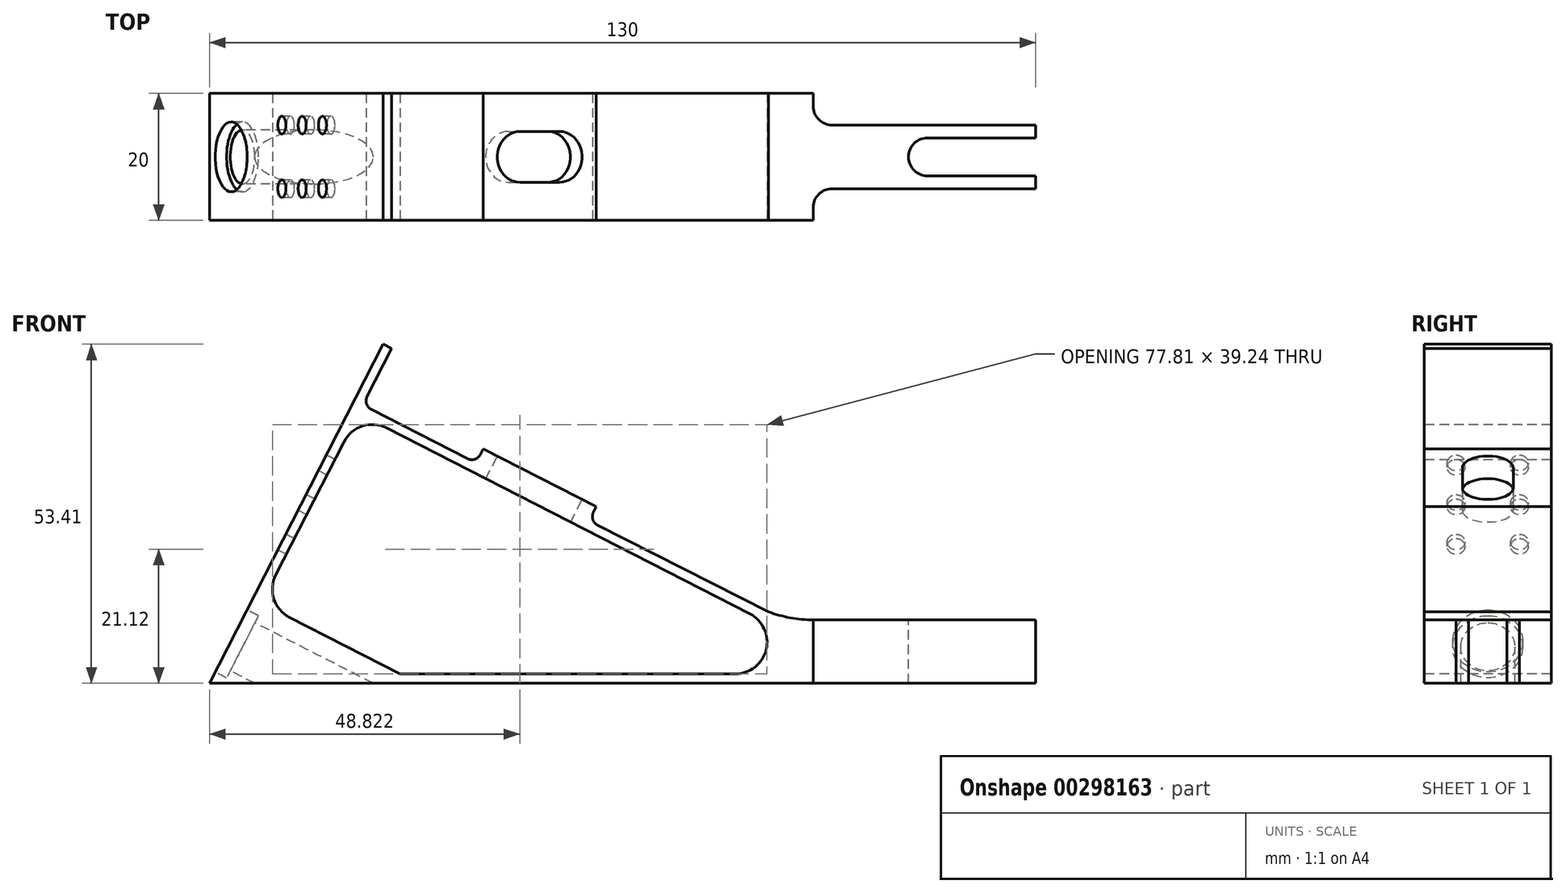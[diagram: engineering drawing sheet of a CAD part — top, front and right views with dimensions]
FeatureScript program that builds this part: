
annotation { "Feature Type Name" : "Feature", "Feature Type Description" : "" }
export const myFeature = defineFeature(function(context is Context, id is Id, definition is map)
    precondition{}
    {
        {
            var Q0;
            Q0=qCreatedBy(makeId("Front.planeOp"),FACE);
            var sketch = newSketch(context, id + "F0", { "sketchPlane" : qUnion([Q0])});
            skLineSegment(sketch, "E0", {"start": v(0, 0) * mm, "end": v(130, 0) * mm});
            skLineSegment(sketch, "E1", {"start": v(130, 0) * mm, "end": v(130, 10) * mm});
            skLineSegment(sketch, "E2", {"start": v(130, 10) * mm, "end": v(95, 10) * mm});
            skArc(sketch, "E3", {"start": v(95, 10) * mm, "mid": v(91.42, 10.32) * mm, "end": v(87.96, 11.28) * mm});
            skLineSegment(sketch, "E4", {"start": v(0, 0) * mm, "end": v(27.35, 53.4) * mm});
            skLineSegment(sketch, "E5", {"start": v(27.35, 53.4) * mm, "end": v(28.68, 52.72) * mm});
            skLineSegment(sketch, "E6", {"start": v(28.68, 52.72) * mm, "end": v(24.12, 43.82) * mm});
            skLineSegment(sketch, "E7", {"start": v(24.12, 43.82) * mm, "end": v(41.93, 34.7) * mm});
            skLineSegment(sketch, "E8", {"start": v(41.93, 34.7) * mm, "end": v(43.06, 36.93) * mm});
            skLineSegment(sketch, "E9", {"start": v(43.06, 36.93) * mm, "end": v(60.87, 27.82) * mm});
            skLineSegment(sketch, "E10", {"start": v(59.73, 25.6) * mm, "end": v(87.96, 11.28) * mm});
            skLineSegment(sketch, "E11", {"start": v(60.87, 27.82) * mm, "end": v(59.73, 25.6) * mm});
            skSolve(sketch);
        }
        {
            var Q0;
            Q0 = qSketchRegion(id + "F0", true);
            extrude(context, id + "F1", {"entities" : qUnion([Q0]), "depth" : 20 * mm});
        }
        {
            var Q0;
            Q0=makeQuery(id+"F1.opExtrude","SWEPT_EDGE",EDGE,{"disambiguationData":[OSD([sQuery(id+"F0.wireOp",EDGE,"E10"),sQuery(id+"F0.wireOp",EDGE,"E11")])]});
            var Q1;
            Q1=makeQuery(id+"F1.opExtrude","SWEPT_EDGE",EDGE,{"disambiguationData":[OSD([sQuery(id+"F0.wireOp",EDGE,"E6"),sQuery(id+"F0.wireOp",EDGE,"E7")])]});
            var Q2;
            Q2=makeQuery(id+"F1.opExtrude","SWEPT_EDGE",EDGE,{"disambiguationData":[OSD([sQuery(id+"F0.wireOp",EDGE,"E7"),sQuery(id+"F0.wireOp",EDGE,"E8")])]});
            fillet(context, id + "F2", {"entities" : qUnion([Q0, Q1, Q2]), "radius" : 1.5 * mm, "tangentPropagation" : true, "allowEdgeOverflow" : false});
        }
        {
            var Q0;
            Q0=makeQuery(id+"F1.opExtrude","SWEPT_FACE",FACE,{"disambiguationData":[OSD([sQuery(id+"F0.wireOp",EDGE,"E2")])]});
            var sketch = newSketch(context, id + "F3", { "sketchPlane" : qUnion([Q0])});
            skLineSegment(sketch, "E12.bottom", {"start": v(130, 0) * mm, "end": v(95, 0) * mm});
            skLineSegment(sketch, "E12.top", {"start": v(130, -5) * mm, "end": v(95, -5) * mm});
            skLineSegment(sketch, "E12.left", {"start": v(130, 0) * mm, "end": v(130, -5) * mm});
            skLineSegment(sketch, "E12.right", {"start": v(95, 0) * mm, "end": v(95, -5) * mm});
            skLineSegment(sketch, "E13.bottom", {"start": v(130, -20) * mm, "end": v(95, -20) * mm});
            skLineSegment(sketch, "E13.top", {"start": v(130, -15) * mm, "end": v(95, -15) * mm});
            skLineSegment(sketch, "E13.left", {"start": v(130, -20) * mm, "end": v(130, -15) * mm});
            skLineSegment(sketch, "E13.right", {"start": v(95, -20) * mm, "end": v(95, -15) * mm});
            skSolve(sketch);
        }
        {
            var Q0;
            Q0=makeQuery(id+"F3.imprint","IMPRINT",FACE,{"disambiguationData":[TD([[makeQuery(id+"F3.imprint","IMPRINT",EDGE,{"derivedFrom":sQuery(id+"F3.wireOp",EDGE,"E12.bottom")}),1.0]])]});
            var Q1;
            Q1=makeQuery(id+"F3.imprint","IMPRINT",FACE,{"disambiguationData":[TD([[makeQuery(id+"F3.imprint","IMPRINT",EDGE,{"derivedFrom":sQuery(id+"F3.wireOp",EDGE,"E13.bottom")}),-1.0]])]});
            extrude(context, id + "F4", {"entities" : qUnion([Q0, Q1]), "operationType" : NewBodyOperationType.REMOVE, "endBound" : BoundingType.THROUGH_ALL, "oppositeDirection" : true, "depth" : 25 * mm});
        }
        {
            var Q0;
            Q0=makeQuery(id+"F4.boolean.opBoolean","COPY",EDGE,{"derivedFrom":makeQuery(id+"F4.opExtrude","SWEPT_EDGE",EDGE,{"disambiguationData":[OSD([sQuery(id+"F0.wireOp",EDGE,"E2"),sQuery(id+"F0.wireOp",EDGE,"E3"),sQuery(id+"F3.wireOp",EDGE,"E13.top"),sQuery(id+"F3.wireOp",EDGE,"E13.right")])]})});
            var Q1;
            Q1=makeQuery(id+"F4.boolean.opBoolean","COPY",EDGE,{"derivedFrom":makeQuery(id+"F4.opExtrude","SWEPT_EDGE",EDGE,{"disambiguationData":[OSD([sQuery(id+"F0.wireOp",EDGE,"E2"),sQuery(id+"F0.wireOp",EDGE,"E3"),sQuery(id+"F3.wireOp",EDGE,"E12.top"),sQuery(id+"F3.wireOp",EDGE,"E12.right")])]})});
            fillet(context, id + "F5", {"entities" : qUnion([Q0, Q1]), "radius" : 3 * mm, "tangentPropagation" : true, "allowEdgeOverflow" : false});
        }
        {
            var Q0;
            Q0=makeQuery(id+"F1.opExtrude","SWEPT_FACE",FACE,{"disambiguationData":[OSD([sQuery(id+"F0.wireOp",EDGE,"E2")])]});
            var sketch = newSketch(context, id + "F6", { "sketchPlane" : qUnion([Q0])});
            skLineSegment(sketch, "E14.bottom", {"start": v(130, -7) * mm, "end": v(113, -7) * mm});
            skLineSegment(sketch, "E14.top", {"start": v(130, -13) * mm, "end": v(113, -13) * mm});
            skLineSegment(sketch, "E14.left", {"start": v(130, -7) * mm, "end": v(130, -13) * mm});
            skArc(sketch, "E15", {"start": v(113, -13) * mm, "mid": v(110, -10) * mm, "end": v(113, -7) * mm});
            skSolve(sketch);
        }
        {
            var Q0;
            Q0=makeQuery(id+"F6.imprint","IMPRINT",FACE,{"disambiguationData":[TD([[makeQuery(id+"F6.imprint","IMPRINT",EDGE,{"derivedFrom":sQuery(id+"F6.wireOp",EDGE,"E14.bottom")}),1.0]])]});
            extrude(context, id + "F7", {"entities" : qUnion([Q0]), "operationType" : NewBodyOperationType.REMOVE, "endBound" : BoundingType.THROUGH_ALL, "oppositeDirection" : true, "depth" : 25 * mm});
        }
        {
            var Q0;
            Q0=makeQuery(id+"F1.opExtrude","SWEPT_FACE",FACE,{"disambiguationData":[OSD([sQuery(id+"F0.wireOp",EDGE,"E9")])]});
            var sketch = newSketch(context, id + "F8", { "sketchPlane" : qUnion([Q0])});
            skLineSegment(sketch, "E16", {"start": v(-33.5, -10) * mm, "end": v(68.03, -10) * mm, "construction": true});
            skPoint(sketch, "E16.startSnap0", {"position": v(21.5, -10) * mm});
            skLineSegment(sketch, "E17", {"start": v(28, -6) * mm, "end": v(35, -6) * mm});
            skLineSegment(sketch, "E18", {"start": v(28, -14) * mm, "end": v(35, -14) * mm});
            skArc(sketch, "E19", {"start": v(28, -6) * mm, "mid": v(24, -10) * mm, "end": v(28, -14) * mm});
            skArc(sketch, "E20", {"start": v(35, -6) * mm, "mid": v(39, -10) * mm, "end": v(35, -14) * mm});
            skSolve(sketch);
        }
        {
            var Q0;
            Q0 = qSketchRegion(id + "F8", true);
            extrude(context, id + "F9", {"entities" : qUnion([Q0]), "operationType" : NewBodyOperationType.REMOVE, "oppositeDirection" : true, "depth" : 4 * mm});
        }
        {
            var Q0;
            Q0=makeQuery(id+"F1.opExtrude","CAP_FACE",FACE,{"disambiguationData":[OSD([sQuery(id+"F0.wireOp",EDGE,"E0"),sQuery(id+"F0.wireOp",EDGE,"E1"),sQuery(id+"F0.wireOp",EDGE,"E2"),sQuery(id+"F0.wireOp",EDGE,"E3"),sQuery(id+"F0.wireOp",EDGE,"E4"),sQuery(id+"F0.wireOp",EDGE,"E5"),sQuery(id+"F0.wireOp",EDGE,"E6"),sQuery(id+"F0.wireOp",EDGE,"E7"),sQuery(id+"F0.wireOp",EDGE,"E8"),sQuery(id+"F0.wireOp",EDGE,"E9"),sQuery(id+"F0.wireOp",EDGE,"E10"),sQuery(id+"F0.wireOp",EDGE,"E11")])],"isStart":false});
            var sketch = newSketch(context, id + "F10", { "sketchPlane" : qUnion([Q0])});
            skLineSegment(sketch, "E21", {"start": v(21.16, 38.04) * mm, "end": v(10.45, 17.12) * mm});
            skLineSegment(sketch, "E22", {"start": v(27.89, 40.2) * mm, "end": v(85.03, 10.95) * mm});
            skLineSegment(sketch, "E23", {"start": v(29.98, 1.5) * mm, "end": v(82.75, 1.5) * mm});
            skArc(sketch, "E24", {"start": v(21.16, 38.04) * mm, "mid": v(24.08, 40.52) * mm, "end": v(27.89, 40.2) * mm});
            skArc(sketch, "E25", {"start": v(85.03, 10.95) * mm, "mid": v(87.61, 5.33) * mm, "end": v(82.75, 1.5) * mm});
            skLineSegment(sketch, "E26", {"start": v(29.98, 1.5) * mm, "end": v(12.62, 10.39) * mm});
            skArc(sketch, "E27", {"start": v(10.45, 17.12) * mm, "mid": v(10.14, 13.3) * mm, "end": v(12.62, 10.39) * mm});
            skSolve(sketch);
        }
        {
            var Q0;
            Q0 = qSketchRegion(id + "F10", true);
            extrude(context, id + "F11", {"entities" : qUnion([Q0]), "operationType" : NewBodyOperationType.REMOVE, "endBound" : BoundingType.THROUGH_ALL, "oppositeDirection" : true, "depth" : 25 * mm});
        }
        {
            var Q0;
            Q0=makeQuery(id+"F1.opExtrude","SWEPT_FACE",FACE,{"disambiguationData":[OSD([sQuery(id+"F0.wireOp",EDGE,"E4")])]});
            var sketch = newSketch(context, id + "F12", { "sketchPlane" : qUnion([Q0])});
            skCircle(sketch, "E28", {"center": v(10, 7.5) * mm, "radius": 5.5 * mm});
            skCircle(sketch, "E29", {"center": v(10, 7.5) * mm, "radius": 4.25 * mm});
            skSolve(sketch);
        }
        {
            var Q0;
            Q0 = qSketchRegion(id + "F12", true);
            extrude(context, id + "F13", {"entities" : qUnion([Q0]), "operationType" : NewBodyOperationType.REMOVE, "oppositeDirection" : true, "depth" : 2 * mm});
        }
        {
            var Q0;
            Q0=makeQuery(id+"F13.boolean.opBoolean","SPLIT",FACE,{"disambiguationData":[TD([makeQuery(id+"F13.opExtrude","SWEPT_FACE",FACE,{"disambiguationData":[OSD([sQuery(id+"F12.wireOp",EDGE,"E29")])]})])],"derivedFrom":makeQuery(id+"F1.opExtrude","SWEPT_FACE",FACE,{"disambiguationData":[OSD([sQuery(id+"F0.wireOp",EDGE,"E4")])]})});
            extrude(context, id + "F14", {"entities" : qUnion([Q0]), "operationType" : NewBodyOperationType.REMOVE, "endBound" : BoundingType.THROUGH_ALL, "oppositeDirection" : true, "depth" : 25 * mm});
        }
        {
            var Q0;
            {var subQ7=sQuery(id+"F0.wireOp",EDGE,"E4");var subQ11=sQuery(id+"F0.wireOp",EDGE,"E0");Q0=makeQuery(id+"F13.boolean.opBoolean","SPLIT",FACE,{"disambiguationData":[TD([makeQuery(id+"F1.opExtrude","SWEPT_FACE",FACE,{"disambiguationData":[OSD([subQ11])]})])],"derivedFrom":makeQuery(id+"F1.opExtrude","SWEPT_FACE",FACE,{"disambiguationData":[OSD([subQ7])]})});}
            var sketch = newSketch(context, id + "F15", { "sketchPlane" : qUnion([Q0])});
            skCircle(sketch, "E30", {"center": v(5, 25) * mm, "radius": 1.4 * mm});
            skCircle(sketch, "E31", {"center": v(5, 39) * mm, "radius": 1.4 * mm});
            skCircle(sketch, "E32", {"center": v(5, 32) * mm, "radius": 1.4 * mm});
            skLineSegment(sketch, "E33", {"start": v(10, 0) * mm, "end": v(10, 64.44) * mm, "construction": true});
            skCircle(sketch, "E34.MirrorC", {"center": v(15, 39) * mm, "radius": 1.4 * mm});
            skCircle(sketch, "E35.MirrorC", {"center": v(15, 32) * mm, "radius": 1.4 * mm});
            skCircle(sketch, "E36.MirrorC", {"center": v(15, 25) * mm, "radius": 1.4 * mm});
            skSolve(sketch);
        }
        {
            var Q0;
            Q0 = qSketchRegion(id + "F15", true);
            extrude(context, id + "F16", {"entities" : qUnion([Q0]), "operationType" : NewBodyOperationType.REMOVE, "oppositeDirection" : true, "depth" : 25 * mm});
        }
    });
